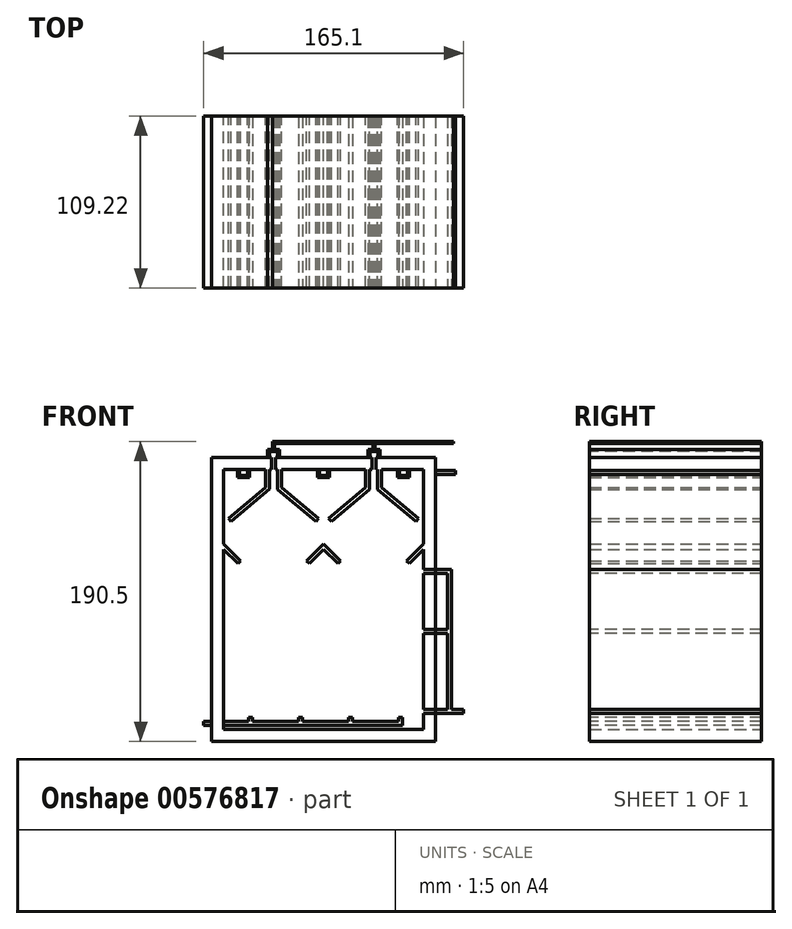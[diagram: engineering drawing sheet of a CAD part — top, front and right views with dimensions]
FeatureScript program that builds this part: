
annotation { "Feature Type Name" : "Feature", "Feature Type Description" : "" }
export const myFeature = defineFeature(function(context is Context, id is Id, definition is map)
    precondition{}
    {
        {
            var Q0;
            Q0=qCreatedBy(makeId("Front.planeOp"),FACE);
            var sketch = newSketch(context, id + "F0", { "sketchPlane" : qUnion([Q0])});
            skLineSegment(sketch, "E0", {"start": v(0, 0) * mm, "end": v(0, 165.1) * mm});
            skLineSegment(sketch, "E1", {"start": v(0, 165.1) * mm, "end": v(127, 165.1) * mm});
            skLineSegment(sketch, "E2", {"start": v(127, 165.1) * mm, "end": v(127, 0) * mm});
            skLineSegment(sketch, "E3", {"start": v(127, 0) * mm, "end": v(0, 0) * mm});
            skLineSegment(sketch, "E4.0", {"start": v(-7.62, -7.62) * mm, "end": v(-7.62, 172.72) * mm});
            skLineSegment(sketch, "E5.0", {"start": v(134.62, -7.62) * mm, "end": v(-7.62, -7.62) * mm});
            skLineSegment(sketch, "E6.0", {"start": v(134.62, 172.72) * mm, "end": v(134.62, -7.62) * mm});
            skLineSegment(sketch, "E7.0", {"start": v(-7.62, 172.72) * mm, "end": v(134.62, 172.72) * mm});
            skSolve(sketch);
        }
        {
            var Q0;
            Q0 = qSketchRegion(id + "F0", true);
            extrude(context, id + "F1", {"entities" : qUnion([Q0]), "depth" : 109.22 * mm, "offsetDistance" : 25.4 * mm});
        }
        {
            var Q0;
            Q0=qCreatedBy(makeId("Front.planeOp"),FACE);
            var sketch = newSketch(context, id + "F2", { "sketchPlane" : qUnion([Q0])});
            skLineSegment(sketch, "E8", {"start": v(0, 0) * mm, "end": v(0, 114.3) * mm, "construction": true});
            skLineSegment(sketch, "E9", {"start": v(34.14, 165.23) * mm, "end": v(34.14, 152.53) * mm});
            skLineSegment(sketch, "E10", {"start": v(34.14, 152.53) * mm, "end": v(58.5, 132.1) * mm});
            skLineSegment(sketch, "E11.0", {"start": v(29.06, 165.23) * mm, "end": v(29.06, 152.61) * mm});
            skLineSegment(sketch, "E12", {"start": v(29.06, 152.61) * mm, "end": v(4.61, 132.1) * mm});
            skLineSegment(sketch, "E13.MirrorCS", {"start": v(92.62, 152.45) * mm, "end": v(68.3, 132.04) * mm});
            skLineSegment(sketch, "E14.MirrorCS", {"start": v(92.62, 165.15) * mm, "end": v(92.62, 152.45) * mm});
            skLineSegment(sketch, "E15.MirrorCS", {"start": v(97.7, 165.14) * mm, "end": v(97.7, 152.44) * mm});
            skLineSegment(sketch, "E16.MirrorCS", {"start": v(97.7, 152.44) * mm, "end": v(122.02, 132.03) * mm});
            skLineSegment(sketch, "E17", {"start": v(0, 114.3) * mm, "end": v(8.98, 105.32) * mm});
            skLineSegment(sketch, "E18.MirrorCS", {"start": v(127, 114.3) * mm, "end": v(118.02, 105.32) * mm});
            skLineSegment(sketch, "E19", {"start": v(63.5, 114.3) * mm, "end": v(54.52, 105.32) * mm});
            skLineSegment(sketch, "E20", {"start": v(63.5, 114.3) * mm, "end": v(72.48, 105.32) * mm});
            skLineSegment(sketch, "E21", {"start": v(63.35, 165.19) * mm, "end": v(63.35, 0) * mm, "construction": true});
            skLineSegment(sketch, "E22.0", {"start": v(0, 117.9) * mm, "end": v(10.78, 107.12) * mm});
            skLineSegment(sketch, "E23.0", {"start": v(127, 117.9) * mm, "end": v(116.22, 107.12) * mm});
            skLineSegment(sketch, "E24.0", {"start": v(63.5, 117.9) * mm, "end": v(52.72, 107.12) * mm});
            skLineSegment(sketch, "E25.0", {"start": v(63.5, 117.9) * mm, "end": v(74.28, 107.12) * mm});
            skLineSegment(sketch, "E26", {"start": v(127, 114.3) * mm, "end": v(127, 121.24) * mm, "construction": true});
            skLineSegment(sketch, "E27", {"start": v(118.02, 105.32) * mm, "end": v(116.22, 107.12) * mm});
            skLineSegment(sketch, "E28", {"start": v(72.48, 105.32) * mm, "end": v(74.28, 107.12) * mm});
            skLineSegment(sketch, "E29", {"start": v(54.52, 105.32) * mm, "end": v(52.72, 107.12) * mm});
            skLineSegment(sketch, "E30", {"start": v(8.98, 105.32) * mm, "end": v(10.78, 107.12) * mm, "construction": true});
            skLineSegment(sketch, "E31.0", {"start": v(90.08, 153.63) * mm, "end": v(66.67, 133.98) * mm});
            skLineSegment(sketch, "E32", {"start": v(0, 165.27) * mm, "end": v(127, 165.1) * mm, "construction": true});
            skLineSegment(sketch, "E33", {"start": v(0, 0) * mm, "end": v(127, 0) * mm, "construction": true});
            skLineSegment(sketch, "E34", {"start": v(127, 165.1) * mm, "end": v(127, 0) * mm, "construction": true});
            skLineSegment(sketch, "E35.0", {"start": v(100.24, 153.62) * mm, "end": v(123.66, 133.98) * mm});
            skLineSegment(sketch, "E36.0", {"start": v(90.08, 165.22) * mm, "end": v(90.08, 153.63) * mm});
            skLineSegment(sketch, "E37.0", {"start": v(100.24, 165.24) * mm, "end": v(100.24, 153.62) * mm});
            skLineSegment(sketch, "E38", {"start": v(66.67, 133.98) * mm, "end": v(68.3, 132.04) * mm});
            skLineSegment(sketch, "E39", {"start": v(122.02, 132.03) * mm, "end": v(123.66, 133.98) * mm});
            skLineSegment(sketch, "E40.MirrorCS", {"start": v(36.6, 153.63) * mm, "end": v(60.02, 133.98) * mm});
            skLineSegment(sketch, "E41.MirrorCS", {"start": v(60.02, 133.98) * mm, "end": v(58.4, 132.04) * mm});
            skLineSegment(sketch, "E42.MirrorCS", {"start": v(36.6, 165.22) * mm, "end": v(36.6, 153.63) * mm});
            skLineSegment(sketch, "E43.MirrorCS", {"start": v(26.45, 165.24) * mm, "end": v(26.45, 153.62) * mm});
            skLineSegment(sketch, "E44.MirrorCS", {"start": v(26.45, 153.62) * mm, "end": v(3.04, 133.98) * mm});
            skLineSegment(sketch, "E45.MirrorCS", {"start": v(4.61, 132.1) * mm, "end": v(3.04, 133.98) * mm});
            skLineSegment(sketch, "E46", {"start": v(0, 165.27) * mm, "end": v(0, 0) * mm, "construction": true});
            skLineSegment(sketch, "E47", {"start": v(8.98, 105.32) * mm, "end": v(10.78, 107.12) * mm});
            skLineSegment(sketch, "E48", {"start": v(127, 114.3) * mm, "end": v(127, 117.9) * mm});
            skLineSegment(sketch, "E49", {"start": v(0, 114.3) * mm, "end": v(0, 117.9) * mm});
            skLineSegment(sketch, "E50", {"start": v(90.08, 165.22) * mm, "end": v(92.62, 165.15) * mm});
            skLineSegment(sketch, "E51", {"start": v(97.7, 165.14) * mm, "end": v(100.24, 165.24) * mm});
            skLineSegment(sketch, "E52", {"start": v(26.45, 165.24) * mm, "end": v(29.06, 165.23) * mm});
            skLineSegment(sketch, "E53", {"start": v(34.14, 165.23) * mm, "end": v(36.6, 165.22) * mm});
            skSolve(sketch);
        }
        {
            var Q0;
            Q0 = qSketchRegion(id + "F2", true);
            extrude(context, id + "F3", {"entities" : qUnion([Q0]), "operationType" : NewBodyOperationType.ADD, "depth" : 109.22 * mm, "offsetDistance" : 25.4 * mm});
        }
        {
            var Q0;
            Q0=qCreatedBy(makeId("Front.planeOp"),FACE);
            var sketch = newSketch(context, id + "F4", { "sketchPlane" : qUnion([Q0])});
            skLineSegment(sketch, "E54.0", {"start": v(36.6, 165.1) * mm, "end": v(90.08, 165.1) * mm, "construction": true});
            skLineSegment(sketch, "E55.2.0.0", {"start": v(161.14, 160.02) * mm, "end": v(161.14, 165.1) * mm});
            skLineSegment(sketch, "E55.2.0.1", {"start": v(164.95, 160.02) * mm, "end": v(168.76, 160.02) * mm});
            skLineSegment(sketch, "E55.2.0.2", {"start": v(164.95, 165.1) * mm, "end": v(164.95, 160.02) * mm, "construction": true});
            skLineSegment(sketch, "E55.2.0.3", {"start": v(168.76, 160.02) * mm, "end": v(168.76, 165.1) * mm});
            skLineSegment(sketch, "E55.2.0.4", {"start": v(164.95, 160.02) * mm, "end": v(161.14, 160.02) * mm});
            skLineSegment(sketch, "E56.1.0.0", {"start": v(16.36, 160.02) * mm, "end": v(16.36, 165.1) * mm});
            skLineSegment(sketch, "E56.1.0.1", {"start": v(12.55, 160.02) * mm, "end": v(16.36, 160.02) * mm});
            skLineSegment(sketch, "E56.1.0.2", {"start": v(8.74, 160.02) * mm, "end": v(8.74, 165.1) * mm});
            skLineSegment(sketch, "E56.1.0.3", {"start": v(12.55, 165.1) * mm, "end": v(12.55, 160.02) * mm, "construction": true});
            skLineSegment(sketch, "E56.1.0.4", {"start": v(12.55, 160.02) * mm, "end": v(8.74, 160.02) * mm});
            skLineSegment(sketch, "E57", {"start": v(8.74, 165.1) * mm, "end": v(10, 165.1) * mm});
            skLineSegment(sketch, "E58", {"start": v(10, 165.1) * mm, "end": v(10, 161.3) * mm});
            skLineSegment(sketch, "E59", {"start": v(10, 161.3) * mm, "end": v(15.09, 161.3) * mm});
            skLineSegment(sketch, "E60", {"start": v(15.09, 161.3) * mm, "end": v(15.09, 165.1) * mm});
            skLineSegment(sketch, "E61", {"start": v(15.09, 165.1) * mm, "end": v(16.36, 165.1) * mm});
            skLineSegment(sketch, "E62.1.0.0", {"start": v(67.16, 160.02) * mm, "end": v(67.16, 165.1) * mm});
            skLineSegment(sketch, "E62.1.0.1", {"start": v(63.35, 165.1) * mm, "end": v(63.35, 160.02) * mm, "construction": true});
            skLineSegment(sketch, "E62.1.0.2", {"start": v(59.54, 160.02) * mm, "end": v(59.54, 165.1) * mm});
            skLineSegment(sketch, "E62.1.0.3", {"start": v(65.89, 161.3) * mm, "end": v(65.89, 165.1) * mm});
            skLineSegment(sketch, "E62.1.0.4", {"start": v(63.35, 160.02) * mm, "end": v(67.16, 160.02) * mm});
            skLineSegment(sketch, "E62.1.0.5", {"start": v(63.35, 160.02) * mm, "end": v(59.54, 160.02) * mm});
            skLineSegment(sketch, "E62.1.0.6", {"start": v(60.8, 161.3) * mm, "end": v(65.89, 161.3) * mm});
            skLineSegment(sketch, "E62.1.0.7", {"start": v(60.8, 165.1) * mm, "end": v(60.8, 161.3) * mm});
            skLineSegment(sketch, "E62.1.0.8", {"start": v(65.89, 165.1) * mm, "end": v(67.16, 165.1) * mm});
            skLineSegment(sketch, "E62.1.0.9", {"start": v(59.54, 165.1) * mm, "end": v(60.8, 165.1) * mm});
            skLineSegment(sketch, "E62.1.0.10", {"start": v(59.54, 165.1) * mm, "end": v(60.8, 165.1) * mm});
            skLineSegment(sketch, "E62.2.0.0", {"start": v(117.96, 160.02) * mm, "end": v(117.96, 165.1) * mm});
            skLineSegment(sketch, "E62.2.0.1", {"start": v(114.15, 165.1) * mm, "end": v(114.15, 160.02) * mm, "construction": true});
            skLineSegment(sketch, "E62.2.0.2", {"start": v(110.34, 160.02) * mm, "end": v(110.34, 165.1) * mm});
            skLineSegment(sketch, "E62.2.0.3", {"start": v(116.69, 161.3) * mm, "end": v(116.69, 165.1) * mm});
            skLineSegment(sketch, "E62.2.0.4", {"start": v(114.15, 160.02) * mm, "end": v(117.96, 160.02) * mm});
            skLineSegment(sketch, "E62.2.0.5", {"start": v(114.15, 160.02) * mm, "end": v(110.34, 160.02) * mm});
            skLineSegment(sketch, "E62.2.0.6", {"start": v(111.6, 161.3) * mm, "end": v(116.69, 161.3) * mm});
            skLineSegment(sketch, "E62.2.0.7", {"start": v(111.6, 165.1) * mm, "end": v(111.6, 161.3) * mm});
            skLineSegment(sketch, "E62.2.0.8", {"start": v(116.69, 165.1) * mm, "end": v(117.96, 165.1) * mm});
            skLineSegment(sketch, "E62.2.0.9", {"start": v(110.34, 165.1) * mm, "end": v(111.6, 165.1) * mm});
            skLineSegment(sketch, "E62.2.0.10", {"start": v(110.34, 165.1) * mm, "end": v(111.6, 165.1) * mm});
            skLineSegment(sketch, "E62.direction1", {"start": v(8.74, 160.02) * mm, "end": v(59.54, 160.02) * mm, "construction": true});
            skSolve(sketch);
        }
        {
            var Q0;
            Q0 = qSketchRegion(id + "F4", true);
            extrude(context, id + "F5", {"entities" : qUnion([Q0]), "depth" : 109.22 * mm, "offsetDistance" : 25.4 * mm});
        }
        {
            var Q0;
            Q0=makeQuery(id+"F3.boolean.opBoolean","MERGE",FACE,{"derivedFrom":[makeQuery(id+"F1.opExtrude","CAP_FACE",FACE,{"disambiguationData":[OSD([sQuery(id+"F0.wireOp",EDGE,"E0"),sQuery(id+"F0.wireOp",EDGE,"E1"),sQuery(id+"F0.wireOp",EDGE,"E2"),sQuery(id+"F0.wireOp",EDGE,"E3"),sQuery(id+"F0.wireOp",EDGE,"E4.0"),sQuery(id+"F0.wireOp",EDGE,"E5.0"),sQuery(id+"F0.wireOp",EDGE,"E6.0"),sQuery(id+"F0.wireOp",EDGE,"E7.0")])],"isStart":false}),makeQuery(id+"F3.opExtrude","CAP_FACE",FACE,{"disambiguationData":[OSD([sQuery(id+"F2.wireOp",EDGE,"E9"),sQuery(id+"F2.wireOp",EDGE,"E10"),sQuery(id+"F2.wireOp",EDGE,"E40.MirrorCS"),sQuery(id+"F2.wireOp",EDGE,"E41.MirrorCS"),sQuery(id+"F2.wireOp",EDGE,"E42.MirrorCS"),sQuery(id+"F2.wireOp",EDGE,"E53")])],"isStart":false}),makeQuery(id+"F3.opExtrude","CAP_FACE",FACE,{"disambiguationData":[OSD([sQuery(id+"F2.wireOp",EDGE,"E11.0"),sQuery(id+"F2.wireOp",EDGE,"E12"),sQuery(id+"F2.wireOp",EDGE,"E43.MirrorCS"),sQuery(id+"F2.wireOp",EDGE,"E44.MirrorCS"),sQuery(id+"F2.wireOp",EDGE,"E45.MirrorCS"),sQuery(id+"F2.wireOp",EDGE,"E52")])],"isStart":false}),makeQuery(id+"F3.opExtrude","CAP_FACE",FACE,{"disambiguationData":[OSD([sQuery(id+"F2.wireOp",EDGE,"E13.MirrorCS"),sQuery(id+"F2.wireOp",EDGE,"E14.MirrorCS"),sQuery(id+"F2.wireOp",EDGE,"E31.0"),sQuery(id+"F2.wireOp",EDGE,"E36.0"),sQuery(id+"F2.wireOp",EDGE,"E38"),sQuery(id+"F2.wireOp",EDGE,"E50")])],"isStart":false}),makeQuery(id+"F3.opExtrude","CAP_FACE",FACE,{"disambiguationData":[OSD([sQuery(id+"F2.wireOp",EDGE,"E15.MirrorCS"),sQuery(id+"F2.wireOp",EDGE,"E16.MirrorCS"),sQuery(id+"F2.wireOp",EDGE,"E35.0"),sQuery(id+"F2.wireOp",EDGE,"E37.0"),sQuery(id+"F2.wireOp",EDGE,"E39"),sQuery(id+"F2.wireOp",EDGE,"E51")])],"isStart":false}),makeQuery(id+"F3.opExtrude","CAP_FACE",FACE,{"disambiguationData":[OSD([sQuery(id+"F2.wireOp",EDGE,"E17"),sQuery(id+"F2.wireOp",EDGE,"E22.0"),sQuery(id+"F2.wireOp",EDGE,"E47"),sQuery(id+"F2.wireOp",EDGE,"E49")])],"isStart":false}),makeQuery(id+"F3.opExtrude","CAP_FACE",FACE,{"disambiguationData":[OSD([sQuery(id+"F2.wireOp",EDGE,"E18.MirrorCS"),sQuery(id+"F2.wireOp",EDGE,"E23.0"),sQuery(id+"F2.wireOp",EDGE,"E27"),sQuery(id+"F2.wireOp",EDGE,"E48")])],"isStart":false})]});
            var sketch = newSketch(context, id + "F6", { "sketchPlane" : qUnion([Q0])});
            skLineSegment(sketch, "E63", {"start": v(63.5, 172.72) * mm, "end": v(31.6, 172.72) * mm, "construction": true});
            skPoint(sketch, "E63.endSnap0", {"position": v(31.6, 165.1) * mm});
            skLineSegment(sketch, "E64", {"start": v(31.6, 172.72) * mm, "end": v(31.6, 165.1) * mm, "construction": true});
            skLineSegment(sketch, "E65.0", {"start": v(32.87, 172.72) * mm, "end": v(32.87, 165.1) * mm});
            skLineSegment(sketch, "E66.MirrorCS", {"start": v(30.33, 172.72) * mm, "end": v(30.33, 165.1) * mm});
            skLineSegment(sketch, "E67", {"start": v(30.33, 172.72) * mm, "end": v(32.87, 172.72) * mm});
            skLineSegment(sketch, "E68", {"start": v(30.33, 165.1) * mm, "end": v(32.87, 165.1) * mm});
            skLineSegment(sketch, "E69", {"start": v(63.5, 172.72) * mm, "end": v(63.5, 165.1) * mm, "construction": true});
            skLineSegment(sketch, "E70.MirrorCS", {"start": v(96.67, 165.1) * mm, "end": v(94.13, 165.1) * mm});
            skLineSegment(sketch, "E71.MirrorCS", {"start": v(96.67, 172.72) * mm, "end": v(94.13, 172.72) * mm});
            skLineSegment(sketch, "E72.MirrorCS", {"start": v(96.67, 172.72) * mm, "end": v(96.67, 165.1) * mm});
            skLineSegment(sketch, "E73.MirrorCS", {"start": v(94.13, 172.72) * mm, "end": v(94.13, 165.1) * mm});
            skLineSegment(sketch, "E74.MirrorCS", {"start": v(95.4, 172.72) * mm, "end": v(95.4, 165.1) * mm, "construction": true});
            skPoint(sketch, "E75.MirrorP", {"position": v(95.4, 165.1) * mm});
            skSolve(sketch);
        }
        {
            var Q0;
            Q0 = qSketchRegion(id + "F6", true);
            extrude(context, id + "F7", {"entities" : qUnion([Q0]), "operationType" : NewBodyOperationType.REMOVE, "endBound" : BoundingType.THROUGH_ALL, "oppositeDirection" : true, "depth" : 25.4 * mm, "offsetDistance" : 25.4 * mm});
        }
        {
            var Q0;
            {var subQ0=sQuery(id+"F2.wireOp",EDGE,"E40.MirrorCS");var subQ1=sQuery(id+"F2.wireOp",EDGE,"E36.0");var subQ2=sQuery(id+"F2.wireOp",EDGE,"E13.MirrorCS");var subQ3=sQuery(id+"F0.wireOp",EDGE,"E1");var subQ4=sQuery(id+"F2.wireOp",EDGE,"E38");var subQ5=sQuery(id+"F0.wireOp",EDGE,"E7.0");var subQ6=sQuery(id+"F2.wireOp",EDGE,"E31.0");var subQ7=sQuery(id+"F2.wireOp",EDGE,"E14.MirrorCS");var subQ8=sQuery(id+"F2.wireOp",EDGE,"E9");var subQ9=sQuery(id+"F2.wireOp",EDGE,"E10");var subQ10=sQuery(id+"F2.wireOp",EDGE,"E41.MirrorCS");var subQ11=sQuery(id+"F2.wireOp",EDGE,"E42.MirrorCS");Q0=makeQuery(id+"F7.boolean.opBoolean","SPLIT",FACE,{"disambiguationData":[TD([makeQuery(id+"F3.opExtrude","SWEPT_FACE",FACE,{"disambiguationData":[OSD([subQ8])]})])],"derivedFrom":makeQuery(id+"F3.boolean.opBoolean","MERGE",FACE,{"derivedFrom":[makeQuery(id+"F1.opExtrude","CAP_FACE",FACE,{"disambiguationData":[OSD([sQuery(id+"F0.wireOp",EDGE,"E0"),subQ3,sQuery(id+"F0.wireOp",EDGE,"E2"),sQuery(id+"F0.wireOp",EDGE,"E3"),sQuery(id+"F0.wireOp",EDGE,"E4.0"),sQuery(id+"F0.wireOp",EDGE,"E5.0"),sQuery(id+"F0.wireOp",EDGE,"E6.0"),subQ5])],"isStart":false}),makeQuery(id+"F3.opExtrude","CAP_FACE",FACE,{"disambiguationData":[OSD([subQ8,subQ9,subQ0,subQ10,subQ11,sQuery(id+"F2.wireOp",EDGE,"E53")])],"isStart":false}),makeQuery(id+"F3.opExtrude","CAP_FACE",FACE,{"disambiguationData":[OSD([sQuery(id+"F2.wireOp",EDGE,"E11.0"),sQuery(id+"F2.wireOp",EDGE,"E12"),sQuery(id+"F2.wireOp",EDGE,"E43.MirrorCS"),sQuery(id+"F2.wireOp",EDGE,"E44.MirrorCS"),sQuery(id+"F2.wireOp",EDGE,"E45.MirrorCS"),sQuery(id+"F2.wireOp",EDGE,"E52")])],"isStart":false}),makeQuery(id+"F3.opExtrude","CAP_FACE",FACE,{"disambiguationData":[OSD([subQ2,subQ7,subQ6,subQ1,subQ4,sQuery(id+"F2.wireOp",EDGE,"E50")])],"isStart":false}),makeQuery(id+"F3.opExtrude","CAP_FACE",FACE,{"disambiguationData":[OSD([sQuery(id+"F2.wireOp",EDGE,"E15.MirrorCS"),sQuery(id+"F2.wireOp",EDGE,"E16.MirrorCS"),sQuery(id+"F2.wireOp",EDGE,"E35.0"),sQuery(id+"F2.wireOp",EDGE,"E37.0"),sQuery(id+"F2.wireOp",EDGE,"E39"),sQuery(id+"F2.wireOp",EDGE,"E51")])],"isStart":false}),makeQuery(id+"F3.opExtrude","CAP_FACE",FACE,{"disambiguationData":[OSD([sQuery(id+"F2.wireOp",EDGE,"E17"),sQuery(id+"F2.wireOp",EDGE,"E22.0"),sQuery(id+"F2.wireOp",EDGE,"E47"),sQuery(id+"F2.wireOp",EDGE,"E49")])],"isStart":false}),makeQuery(id+"F3.opExtrude","CAP_FACE",FACE,{"disambiguationData":[OSD([sQuery(id+"F2.wireOp",EDGE,"E18.MirrorCS"),sQuery(id+"F2.wireOp",EDGE,"E23.0"),sQuery(id+"F2.wireOp",EDGE,"E27"),sQuery(id+"F2.wireOp",EDGE,"E48")])],"isStart":false})]})});}
            var sketch = newSketch(context, id + "F8", { "sketchPlane" : qUnion([Q0])});
            skLineSegment(sketch, "E76", {"start": v(32.87, 172.72) * mm, "end": v(35.4, 172.72) * mm});
            skLineSegment(sketch, "E77", {"start": v(35.4, 172.72) * mm, "end": v(35.4, 177.8) * mm});
            skLineSegment(sketch, "E78", {"start": v(35.4, 177.8) * mm, "end": v(34.14, 177.8) * mm});
            skLineSegment(sketch, "E79", {"start": v(34.14, 177.8) * mm, "end": v(29.06, 177.8) * mm});
            skLineSegment(sketch, "E80", {"start": v(29.06, 177.8) * mm, "end": v(27.79, 177.8) * mm});
            skLineSegment(sketch, "E81", {"start": v(27.79, 177.8) * mm, "end": v(27.79, 172.72) * mm});
            skLineSegment(sketch, "E82", {"start": v(27.79, 172.72) * mm, "end": v(29.06, 172.72) * mm});
            skLineSegment(sketch, "E83", {"start": v(29.06, 172.72) * mm, "end": v(29.06, 176.53) * mm});
            skLineSegment(sketch, "E84", {"start": v(29.06, 176.53) * mm, "end": v(34.14, 176.53) * mm});
            skLineSegment(sketch, "E85", {"start": v(34.14, 176.53) * mm, "end": v(34.14, 172.72) * mm});
            skLineSegment(sketch, "E86", {"start": v(63.5, 172.72) * mm, "end": v(63.5, 177.8) * mm, "construction": true});
            skLineSegment(sketch, "E87.MirrorCS", {"start": v(91.6, 177.8) * mm, "end": v(92.86, 177.8) * mm});
            skLineSegment(sketch, "E88.MirrorCS", {"start": v(97.94, 177.8) * mm, "end": v(99.21, 177.8) * mm});
            skLineSegment(sketch, "E89.MirrorCS", {"start": v(99.21, 172.72) * mm, "end": v(97.94, 172.72) * mm});
            skLineSegment(sketch, "E90.MirrorCS", {"start": v(94.13, 172.72) * mm, "end": v(91.6, 172.72) * mm});
            skLineSegment(sketch, "E91.MirrorCS", {"start": v(91.6, 172.72) * mm, "end": v(91.6, 177.8) * mm});
            skLineSegment(sketch, "E92.MirrorCS", {"start": v(92.86, 176.53) * mm, "end": v(92.86, 172.72) * mm});
            skLineSegment(sketch, "E93.MirrorCS", {"start": v(97.94, 176.53) * mm, "end": v(92.86, 176.53) * mm});
            skLineSegment(sketch, "E94.MirrorCS", {"start": v(99.21, 177.8) * mm, "end": v(99.21, 172.72) * mm});
            skLineSegment(sketch, "E95.MirrorCS", {"start": v(97.94, 172.72) * mm, "end": v(97.94, 176.53) * mm});
            skLineSegment(sketch, "E96.MirrorCS", {"start": v(92.86, 177.8) * mm, "end": v(97.94, 177.8) * mm});
            skSolve(sketch);
        }
        {
            var Q0;
            Q0 = qSketchRegion(id + "F8", true);
            extrude(context, id + "F9", {"entities" : qUnion([Q0]), "oppositeDirection" : true, "depth" : 109.22 * mm, "offsetDistance" : 25.4 * mm});
        }
        {
            var Q0;
            {var subQ0=sQuery(id+"F2.wireOp",EDGE,"E44.MirrorCS");var subQ1=sQuery(id+"F2.wireOp",EDGE,"E35.0");var subQ2=sQuery(id+"F2.wireOp",EDGE,"E22.0");var subQ3=sQuery(id+"F2.wireOp",EDGE,"E15.MirrorCS");var subQ4=sQuery(id+"F0.wireOp",EDGE,"E2");var subQ5=sQuery(id+"F2.wireOp",EDGE,"E47");var subQ6=sQuery(id+"F2.wireOp",EDGE,"E37.0");var subQ7=sQuery(id+"F0.wireOp",EDGE,"E1");var subQ8=sQuery(id+"F2.wireOp",EDGE,"E45.MirrorCS");var subQ9=sQuery(id+"F2.wireOp",EDGE,"E39");var subQ10=sQuery(id+"F2.wireOp",EDGE,"E16.MirrorCS");var subQ11=sQuery(id+"F0.wireOp",EDGE,"E3");var subQ12=sQuery(id+"F0.wireOp",EDGE,"E0");var subQ13=sQuery(id+"F2.wireOp",EDGE,"E17");var subQ14=sQuery(id+"F0.wireOp",EDGE,"E4.0");var subQ15=sQuery(id+"F0.wireOp",EDGE,"E5.0");var subQ16=sQuery(id+"F0.wireOp",EDGE,"E6.0");var subQ17=sQuery(id+"F2.wireOp",EDGE,"E43.MirrorCS");var subQ18=sQuery(id+"F2.wireOp",EDGE,"E18.MirrorCS");var subQ19=sQuery(id+"F0.wireOp",EDGE,"E7.0");var subQ20=sQuery(id+"F2.wireOp",EDGE,"E23.0");var subQ21=sQuery(id+"F2.wireOp",EDGE,"E11.0");var subQ22=sQuery(id+"F2.wireOp",EDGE,"E27");var subQ23=sQuery(id+"F2.wireOp",EDGE,"E12");Q0=makeQuery(id+"F7.boolean.opBoolean","SPLIT",FACE,{"disambiguationData":[TD([makeQuery(id+"F1.opExtrude","SWEPT_FACE",FACE,{"disambiguationData":[OSD([subQ12])]})])],"derivedFrom":makeQuery(id+"F3.boolean.opBoolean","MERGE",FACE,{"derivedFrom":[makeQuery(id+"F1.opExtrude","CAP_FACE",FACE,{"disambiguationData":[OSD([subQ12,subQ7,subQ4,subQ11,subQ14,subQ15,subQ16,subQ19])],"isStart":false}),makeQuery(id+"F3.opExtrude","CAP_FACE",FACE,{"disambiguationData":[OSD([sQuery(id+"F2.wireOp",EDGE,"E9"),sQuery(id+"F2.wireOp",EDGE,"E10"),sQuery(id+"F2.wireOp",EDGE,"E40.MirrorCS"),sQuery(id+"F2.wireOp",EDGE,"E41.MirrorCS"),sQuery(id+"F2.wireOp",EDGE,"E42.MirrorCS"),sQuery(id+"F2.wireOp",EDGE,"E53")])],"isStart":false}),makeQuery(id+"F3.opExtrude","CAP_FACE",FACE,{"disambiguationData":[OSD([subQ21,subQ23,subQ17,subQ0,subQ8,sQuery(id+"F2.wireOp",EDGE,"E52")])],"isStart":false}),makeQuery(id+"F3.opExtrude","CAP_FACE",FACE,{"disambiguationData":[OSD([sQuery(id+"F2.wireOp",EDGE,"E13.MirrorCS"),sQuery(id+"F2.wireOp",EDGE,"E14.MirrorCS"),sQuery(id+"F2.wireOp",EDGE,"E31.0"),sQuery(id+"F2.wireOp",EDGE,"E36.0"),sQuery(id+"F2.wireOp",EDGE,"E38"),sQuery(id+"F2.wireOp",EDGE,"E50")])],"isStart":false}),makeQuery(id+"F3.opExtrude","CAP_FACE",FACE,{"disambiguationData":[OSD([subQ3,subQ10,subQ1,subQ6,subQ9,sQuery(id+"F2.wireOp",EDGE,"E51")])],"isStart":false}),makeQuery(id+"F3.opExtrude","CAP_FACE",FACE,{"disambiguationData":[OSD([subQ13,subQ2,subQ5,sQuery(id+"F2.wireOp",EDGE,"E49")])],"isStart":false}),makeQuery(id+"F3.opExtrude","CAP_FACE",FACE,{"disambiguationData":[OSD([subQ18,subQ20,subQ22,sQuery(id+"F2.wireOp",EDGE,"E48")])],"isStart":false})]})});}
            var sketch = newSketch(context, id + "F10", { "sketchPlane" : qUnion([Q0])});
            skLineSegment(sketch, "E97.top", {"start": v(1.16, 2.54) * mm, "end": v(113.56, 2.54) * mm});
            skLineSegment(sketch, "E98.top", {"start": v(1.16, 5.08) * mm, "end": v(113.56, 5.08) * mm});
            skLineSegment(sketch, "E99", {"start": v(1.16, 5.08) * mm, "end": v(17.04, 5.08) * mm});
            skLineSegment(sketch, "E100", {"start": v(17.04, 5.08) * mm, "end": v(48.79, 5.08) * mm});
            skLineSegment(sketch, "E101", {"start": v(48.79, 5.08) * mm, "end": v(80.54, 5.08) * mm});
            skLineSegment(sketch, "E102", {"start": v(80.54, 5.08) * mm, "end": v(112.29, 5.08) * mm});
            skLineSegment(sketch, "E103", {"start": v(17.04, 5.08) * mm, "end": v(15.77, 5.08) * mm});
            skLineSegment(sketch, "E104", {"start": v(15.77, 5.08) * mm, "end": v(15.77, 7.62) * mm});
            skLineSegment(sketch, "E105", {"start": v(15.77, 7.62) * mm, "end": v(18.3, 7.62) * mm});
            skLineSegment(sketch, "E106", {"start": v(18.3, 7.62) * mm, "end": v(18.3, 5.08) * mm});
            skLineSegment(sketch, "E107.1.0.0", {"start": v(47.52, 7.62) * mm, "end": v(50.06, 7.62) * mm});
            skLineSegment(sketch, "E107.1.0.1", {"start": v(47.52, 5.08) * mm, "end": v(47.52, 7.62) * mm});
            skLineSegment(sketch, "E107.1.0.2", {"start": v(50.06, 7.62) * mm, "end": v(50.06, 5.08) * mm});
            skLineSegment(sketch, "E107.2.0.0", {"start": v(79.27, 7.62) * mm, "end": v(81.8, 7.62) * mm});
            skLineSegment(sketch, "E107.2.0.1", {"start": v(79.27, 5.08) * mm, "end": v(79.27, 7.62) * mm});
            skLineSegment(sketch, "E107.2.0.2", {"start": v(81.8, 7.62) * mm, "end": v(81.8, 5.08) * mm});
            skLineSegment(sketch, "E107.3.0.0", {"start": v(111.02, 7.62) * mm, "end": v(113.56, 7.62) * mm});
            skLineSegment(sketch, "E107.3.0.1", {"start": v(111.02, 5.08) * mm, "end": v(111.02, 7.62) * mm});
            skLineSegment(sketch, "E107.3.0.2", {"start": v(113.56, 7.62) * mm, "end": v(113.56, 5.08) * mm});
            skLineSegment(sketch, "E107.direction1", {"start": v(15.77, 7.62) * mm, "end": v(47.52, 7.62) * mm, "construction": true});
            skLineSegment(sketch, "E108", {"start": v(1.16, 2.54) * mm, "end": v(0, 2.54) * mm});
            skLineSegment(sketch, "E109", {"start": v(0, 2.54) * mm, "end": v(0, 5.08) * mm});
            skLineSegment(sketch, "E110", {"start": v(0, 5.08) * mm, "end": v(1.16, 5.08) * mm});
            skLineSegment(sketch, "E111", {"start": v(113.56, 5.08) * mm, "end": v(113.56, 2.54) * mm});
            skLineSegment(sketch, "E112", {"start": v(-7.62, 5.08) * mm, "end": v(-12.7, 5.08) * mm});
            skLineSegment(sketch, "E113", {"start": v(-12.7, 5.08) * mm, "end": v(-12.7, 2.54) * mm});
            skLineSegment(sketch, "E114", {"start": v(-12.7, 2.54) * mm, "end": v(-7.62, 2.54) * mm});
            skLineSegment(sketch, "E115", {"start": v(-7.62, 2.54) * mm, "end": v(-7.62, 5.08) * mm});
            skSolve(sketch);
        }
        {
            var Q0;
            Q0 = qSketchRegion(id + "F10", true);
            extrude(context, id + "F11", {"entities" : qUnion([Q0]), "oppositeDirection" : true, "depth" : 109.22 * mm, "offsetDistance" : 25.4 * mm});
        }
        {
            var Q0;
            {var subQ0=sQuery(id+"F2.wireOp",EDGE,"E44.MirrorCS");var subQ1=sQuery(id+"F2.wireOp",EDGE,"E35.0");var subQ2=sQuery(id+"F2.wireOp",EDGE,"E22.0");var subQ3=sQuery(id+"F2.wireOp",EDGE,"E15.MirrorCS");var subQ4=sQuery(id+"F0.wireOp",EDGE,"E2");var subQ5=sQuery(id+"F2.wireOp",EDGE,"E47");var subQ6=sQuery(id+"F2.wireOp",EDGE,"E37.0");var subQ7=sQuery(id+"F0.wireOp",EDGE,"E1");var subQ8=sQuery(id+"F2.wireOp",EDGE,"E45.MirrorCS");var subQ9=sQuery(id+"F2.wireOp",EDGE,"E39");var subQ10=sQuery(id+"F2.wireOp",EDGE,"E16.MirrorCS");var subQ11=sQuery(id+"F0.wireOp",EDGE,"E3");var subQ12=sQuery(id+"F0.wireOp",EDGE,"E0");var subQ13=sQuery(id+"F2.wireOp",EDGE,"E17");var subQ14=sQuery(id+"F0.wireOp",EDGE,"E4.0");var subQ15=sQuery(id+"F0.wireOp",EDGE,"E5.0");var subQ16=sQuery(id+"F0.wireOp",EDGE,"E6.0");var subQ17=sQuery(id+"F2.wireOp",EDGE,"E43.MirrorCS");var subQ18=sQuery(id+"F2.wireOp",EDGE,"E18.MirrorCS");var subQ19=sQuery(id+"F0.wireOp",EDGE,"E7.0");var subQ20=sQuery(id+"F2.wireOp",EDGE,"E23.0");var subQ21=sQuery(id+"F2.wireOp",EDGE,"E11.0");var subQ22=sQuery(id+"F2.wireOp",EDGE,"E27");var subQ23=sQuery(id+"F2.wireOp",EDGE,"E12");Q0=makeQuery(id+"F11.boolean.opBoolean","MERGE",FACE,{"derivedFrom":[makeQuery(id+"F7.boolean.opBoolean","SPLIT",FACE,{"disambiguationData":[TD([makeQuery(id+"F1.opExtrude","SWEPT_FACE",FACE,{"disambiguationData":[OSD([subQ12])]})])],"derivedFrom":makeQuery(id+"F3.boolean.opBoolean","MERGE",FACE,{"derivedFrom":[makeQuery(id+"F1.opExtrude","CAP_FACE",FACE,{"disambiguationData":[OSD([subQ12,subQ7,subQ4,subQ11,subQ14,subQ15,subQ16,subQ19])],"isStart":false}),makeQuery(id+"F3.opExtrude","CAP_FACE",FACE,{"disambiguationData":[OSD([sQuery(id+"F2.wireOp",EDGE,"E9"),sQuery(id+"F2.wireOp",EDGE,"E10"),sQuery(id+"F2.wireOp",EDGE,"E40.MirrorCS"),sQuery(id+"F2.wireOp",EDGE,"E41.MirrorCS"),sQuery(id+"F2.wireOp",EDGE,"E42.MirrorCS"),sQuery(id+"F2.wireOp",EDGE,"E53")])],"isStart":false}),makeQuery(id+"F3.opExtrude","CAP_FACE",FACE,{"disambiguationData":[OSD([subQ21,subQ23,subQ17,subQ0,subQ8,sQuery(id+"F2.wireOp",EDGE,"E52")])],"isStart":false}),makeQuery(id+"F3.opExtrude","CAP_FACE",FACE,{"disambiguationData":[OSD([sQuery(id+"F2.wireOp",EDGE,"E13.MirrorCS"),sQuery(id+"F2.wireOp",EDGE,"E14.MirrorCS"),sQuery(id+"F2.wireOp",EDGE,"E31.0"),sQuery(id+"F2.wireOp",EDGE,"E36.0"),sQuery(id+"F2.wireOp",EDGE,"E38"),sQuery(id+"F2.wireOp",EDGE,"E50")])],"isStart":false}),makeQuery(id+"F3.opExtrude","CAP_FACE",FACE,{"disambiguationData":[OSD([subQ3,subQ10,subQ1,subQ6,subQ9,sQuery(id+"F2.wireOp",EDGE,"E51")])],"isStart":false}),makeQuery(id+"F3.opExtrude","CAP_FACE",FACE,{"disambiguationData":[OSD([subQ13,subQ2,subQ5,sQuery(id+"F2.wireOp",EDGE,"E49")])],"isStart":false}),makeQuery(id+"F3.opExtrude","CAP_FACE",FACE,{"disambiguationData":[OSD([subQ18,subQ20,subQ22,sQuery(id+"F2.wireOp",EDGE,"E48")])],"isStart":false})]})}),makeQuery(id+"F11.opExtrude","CAP_FACE",FACE,{"disambiguationData":[OSD([sQuery(id+"F10.wireOp",EDGE,"E97.top"),sQuery(id+"F10.wireOp",EDGE,"E98.top"),sQuery(id+"F10.wireOp",EDGE,"E98.left"),sQuery(id+"F10.wireOp",EDGE,"E98.right"),sQuery(id+"F10.wireOp",EDGE,"E99"),sQuery(id+"F10.wireOp",EDGE,"E100"),sQuery(id+"F10.wireOp",EDGE,"E101"),sQuery(id+"F10.wireOp",EDGE,"E102"),sQuery(id+"F10.wireOp",EDGE,"E104"),sQuery(id+"F10.wireOp",EDGE,"E105"),sQuery(id+"F10.wireOp",EDGE,"E106"),sQuery(id+"F10.wireOp",EDGE,"E107.1.0.0"),sQuery(id+"F10.wireOp",EDGE,"E107.1.0.1"),sQuery(id+"F10.wireOp",EDGE,"E107.1.0.2"),sQuery(id+"F10.wireOp",EDGE,"E107.2.0.0"),sQuery(id+"F10.wireOp",EDGE,"E107.2.0.1"),sQuery(id+"F10.wireOp",EDGE,"E107.2.0.2"),sQuery(id+"F10.wireOp",EDGE,"E107.3.0.0"),sQuery(id+"F10.wireOp",EDGE,"E107.3.0.1"),sQuery(id+"F10.wireOp",EDGE,"E107.3.0.2")])],"isStart":true})]});}
            var sketch = newSketch(context, id + "F12", { "sketchPlane" : qUnion([Q0])});
            skLineSegment(sketch, "E116", {"start": v(127, 5.08) * mm, "end": v(127, 10.16) * mm});
            skLineSegment(sketch, "E117", {"start": v(127, 10.16) * mm, "end": v(134.62, 10.16) * mm});
            skLineSegment(sketch, "E118", {"start": v(134.62, 10.16) * mm, "end": v(134.62, 12.7) * mm});
            skLineSegment(sketch, "E119", {"start": v(134.62, 12.7) * mm, "end": v(127, 12.7) * mm});
            skLineSegment(sketch, "E120", {"start": v(127, 12.7) * mm, "end": v(127, 10.16) * mm});
            skLineSegment(sketch, "E121.direction1", {"start": v(127, 10.16) * mm, "end": v(127, 10.16) * mm});
            skLineSegment(sketch, "E121.direction2", {"start": v(127, 10.16) * mm, "end": v(127, 60.96) * mm, "construction": true});
            skLineSegment(sketch, "E122.0.0.1", {"start": v(127, 60.96) * mm, "end": v(134.62, 60.96) * mm});
            skLineSegment(sketch, "E122.3.0.1", {"start": v(134.62, 60.96) * mm, "end": v(134.62, 63.5) * mm});
            skLineSegment(sketch, "E122.6.0.1", {"start": v(134.62, 63.5) * mm, "end": v(127, 63.5) * mm});
            skLineSegment(sketch, "E122.9.0.1", {"start": v(127, 63.5) * mm, "end": v(127, 60.96) * mm});
            skLineSegment(sketch, "E122.0.1.1", {"start": v(127, 60.96) * mm, "end": v(134.62, 60.96) * mm});
            skLineSegment(sketch, "E122.3.1.1", {"start": v(134.62, 60.96) * mm, "end": v(134.62, 63.5) * mm});
            skLineSegment(sketch, "E122.6.1.1", {"start": v(134.62, 63.5) * mm, "end": v(127, 63.5) * mm});
            skLineSegment(sketch, "E122.9.1.1", {"start": v(127, 63.5) * mm, "end": v(127, 60.96) * mm});
            skLineSegment(sketch, "E122.0.2.1", {"start": v(127, 60.96) * mm, "end": v(134.62, 60.96) * mm});
            skLineSegment(sketch, "E122.3.2.1", {"start": v(134.62, 60.96) * mm, "end": v(134.62, 63.5) * mm});
            skLineSegment(sketch, "E122.6.2.1", {"start": v(134.62, 63.5) * mm, "end": v(127, 63.5) * mm});
            skLineSegment(sketch, "E122.9.2.1", {"start": v(127, 63.5) * mm, "end": v(127, 60.96) * mm});
            skLineSegment(sketch, "E123.0.1.0", {"start": v(127, 99.06) * mm, "end": v(134.62, 99.06) * mm});
            skLineSegment(sketch, "E123.0.1.1", {"start": v(134.62, 101.6) * mm, "end": v(127, 101.6) * mm});
            skLineSegment(sketch, "E123.0.1.2", {"start": v(134.62, 101.6) * mm, "end": v(127, 101.6) * mm});
            skLineSegment(sketch, "E123.0.1.3", {"start": v(127, 99.06) * mm, "end": v(134.62, 99.06) * mm});
            skLineSegment(sketch, "E123.0.1.4", {"start": v(134.62, 101.6) * mm, "end": v(127, 101.6) * mm});
            skLineSegment(sketch, "E123.0.1.5", {"start": v(127, 99.06) * mm, "end": v(134.62, 99.06) * mm});
            skLineSegment(sketch, "E123.0.1.6", {"start": v(134.62, 99.06) * mm, "end": v(134.62, 101.6) * mm});
            skLineSegment(sketch, "E123.0.1.7", {"start": v(127, 101.6) * mm, "end": v(127, 99.06) * mm});
            skLineSegment(sketch, "E123.0.1.8", {"start": v(127, 101.6) * mm, "end": v(127, 99.06) * mm});
            skLineSegment(sketch, "E123.0.1.9", {"start": v(134.62, 99.06) * mm, "end": v(134.62, 101.6) * mm});
            skLineSegment(sketch, "E123.0.1.10", {"start": v(134.62, 99.06) * mm, "end": v(134.62, 101.6) * mm});
            skLineSegment(sketch, "E123.0.1.11", {"start": v(127, 101.6) * mm, "end": v(127, 99.06) * mm});
            skLineSegment(sketch, "E123.1.1.0", {"start": v(127, 99.06) * mm, "end": v(134.62, 99.06) * mm});
            skLineSegment(sketch, "E123.1.1.1", {"start": v(134.62, 101.6) * mm, "end": v(127, 101.6) * mm});
            skLineSegment(sketch, "E123.1.1.2", {"start": v(134.62, 101.6) * mm, "end": v(127, 101.6) * mm});
            skLineSegment(sketch, "E123.1.1.3", {"start": v(127, 99.06) * mm, "end": v(134.62, 99.06) * mm});
            skLineSegment(sketch, "E123.1.1.4", {"start": v(134.62, 101.6) * mm, "end": v(127, 101.6) * mm});
            skLineSegment(sketch, "E123.1.1.5", {"start": v(127, 99.06) * mm, "end": v(134.62, 99.06) * mm});
            skLineSegment(sketch, "E123.1.1.6", {"start": v(134.62, 99.06) * mm, "end": v(134.62, 101.6) * mm});
            skLineSegment(sketch, "E123.1.1.7", {"start": v(127, 101.6) * mm, "end": v(127, 99.06) * mm});
            skLineSegment(sketch, "E123.1.1.8", {"start": v(127, 101.6) * mm, "end": v(127, 99.06) * mm});
            skLineSegment(sketch, "E123.1.1.9", {"start": v(134.62, 99.06) * mm, "end": v(134.62, 101.6) * mm});
            skLineSegment(sketch, "E123.1.1.10", {"start": v(134.62, 99.06) * mm, "end": v(134.62, 101.6) * mm});
            skLineSegment(sketch, "E123.1.1.11", {"start": v(127, 101.6) * mm, "end": v(127, 99.06) * mm});
            skLineSegment(sketch, "E123.2.1.0", {"start": v(127, 99.06) * mm, "end": v(134.62, 99.06) * mm});
            skLineSegment(sketch, "E123.2.1.1", {"start": v(134.62, 101.6) * mm, "end": v(127, 101.6) * mm});
            skLineSegment(sketch, "E123.2.1.2", {"start": v(134.62, 101.6) * mm, "end": v(127, 101.6) * mm});
            skLineSegment(sketch, "E123.2.1.3", {"start": v(127, 99.06) * mm, "end": v(134.62, 99.06) * mm});
            skLineSegment(sketch, "E123.2.1.4", {"start": v(134.62, 101.6) * mm, "end": v(127, 101.6) * mm});
            skLineSegment(sketch, "E123.2.1.5", {"start": v(127, 99.06) * mm, "end": v(134.62, 99.06) * mm});
            skLineSegment(sketch, "E123.2.1.6", {"start": v(134.62, 99.06) * mm, "end": v(134.62, 101.6) * mm});
            skLineSegment(sketch, "E123.2.1.7", {"start": v(127, 101.6) * mm, "end": v(127, 99.06) * mm});
            skLineSegment(sketch, "E123.2.1.8", {"start": v(127, 101.6) * mm, "end": v(127, 99.06) * mm});
            skLineSegment(sketch, "E123.2.1.9", {"start": v(134.62, 99.06) * mm, "end": v(134.62, 101.6) * mm});
            skLineSegment(sketch, "E123.2.1.10", {"start": v(134.62, 99.06) * mm, "end": v(134.62, 101.6) * mm});
            skLineSegment(sketch, "E123.2.1.11", {"start": v(127, 101.6) * mm, "end": v(127, 99.06) * mm});
            skLineSegment(sketch, "E123.direction1", {"start": v(127, 60.96) * mm, "end": v(127, 60.96) * mm});
            skLineSegment(sketch, "E123.direction2", {"start": v(127, 60.96) * mm, "end": v(127, 99.06) * mm, "construction": true});
            skSolve(sketch);
        }
        {
            var Q0;
            Q0 = qSketchRegion(id + "F12", true);
            extrude(context, id + "F13", {"entities" : qUnion([Q0]), "operationType" : NewBodyOperationType.REMOVE, "endBound" : BoundingType.THROUGH_ALL, "oppositeDirection" : true, "depth" : 25.4 * mm, "offsetDistance" : 25.4 * mm});
        }
        {
            var Q0;
            Q0=makeQuery(id+"F9.opExtrude","CAP_FACE",FACE,{"disambiguationData":[OSD([sQuery(id+"F8.wireOp",EDGE,"E76"),sQuery(id+"F8.wireOp",EDGE,"E77"),sQuery(id+"F8.wireOp",EDGE,"E78"),sQuery(id+"F8.wireOp",EDGE,"E79"),sQuery(id+"F8.wireOp",EDGE,"E80"),sQuery(id+"F8.wireOp",EDGE,"E81"),sQuery(id+"F8.wireOp",EDGE,"E82"),sQuery(id+"F8.wireOp",EDGE,"E83"),sQuery(id+"F8.wireOp",EDGE,"E84"),sQuery(id+"F8.wireOp",EDGE,"E85")])],"isStart":true});
            var sketch = newSketch(context, id + "F14", { "sketchPlane" : qUnion([Q0])});
            skLineSegment(sketch, "E124", {"start": v(31.6, 177.8) * mm, "end": v(31.6, 182.88) * mm, "construction": true});
            skLineSegment(sketch, "E125", {"start": v(31.6, 182.88) * mm, "end": v(145.9, 182.88) * mm});
            skLineSegment(sketch, "E126", {"start": v(31.6, 182.88) * mm, "end": v(30.96, 182.88) * mm, "construction": true});
            skLineSegment(sketch, "E127", {"start": v(30.96, 182.88) * mm, "end": v(30.96, 177.8) * mm});
            skLineSegment(sketch, "E128", {"start": v(30.96, 177.8) * mm, "end": v(32.23, 177.8) * mm});
            skLineSegment(sketch, "E129", {"start": v(32.23, 177.8) * mm, "end": v(32.23, 181.61) * mm});
            skLineSegment(sketch, "E130", {"start": v(32.23, 181.61) * mm, "end": v(94.77, 181.61) * mm});
            skLineSegment(sketch, "E131", {"start": v(145.9, 181.61) * mm, "end": v(145.9, 182.88) * mm});
            skLineSegment(sketch, "E132", {"start": v(95.4, 177.8) * mm, "end": v(95.4, 181.61) * mm, "construction": true});
            skLineSegment(sketch, "E133", {"start": v(96.04, 181.61) * mm, "end": v(96.04, 177.8) * mm});
            skLineSegment(sketch, "E134", {"start": v(94.77, 177.8) * mm, "end": v(94.77, 181.61) * mm});
            skLineSegment(sketch, "E135.trimOffspring", {"start": v(95.4, 181.61) * mm, "end": v(145.9, 181.61) * mm});
            skLineSegment(sketch, "E136", {"start": v(94.77, 177.8) * mm, "end": v(96.04, 177.8) * mm});
            skLineSegment(sketch, "E137", {"start": v(32.23, 177.8) * mm, "end": v(30.96, 177.8) * mm});
            skLineSegment(sketch, "E138", {"start": v(31.6, 182.88) * mm, "end": v(30.96, 182.88) * mm});
            skSolve(sketch);
        }
        {
            var Q0;
            Q0 = qSketchRegion(id + "F14", true);
            extrude(context, id + "F15", {"entities" : qUnion([Q0]), "oppositeDirection" : true, "depth" : 109.22 * mm, "offsetDistance" : 25.4 * mm});
        }
        {
            var Q0;
            {var subQ0=sQuery(id+"F0.wireOp",EDGE,"E2");var subQ2=sQuery(id+"F0.wireOp",EDGE,"E6.0");var subQ4=sQuery(id+"F2.wireOp",EDGE,"E44.MirrorCS");var subQ5=sQuery(id+"F2.wireOp",EDGE,"E35.0");var subQ6=sQuery(id+"F2.wireOp",EDGE,"E22.0");var subQ7=sQuery(id+"F2.wireOp",EDGE,"E15.MirrorCS");var subQ8=sQuery(id+"F2.wireOp",EDGE,"E47");var subQ9=sQuery(id+"F2.wireOp",EDGE,"E37.0");var subQ10=sQuery(id+"F0.wireOp",EDGE,"E1");var subQ11=sQuery(id+"F2.wireOp",EDGE,"E45.MirrorCS");var subQ12=sQuery(id+"F2.wireOp",EDGE,"E39");var subQ13=sQuery(id+"F2.wireOp",EDGE,"E16.MirrorCS");var subQ14=sQuery(id+"F0.wireOp",EDGE,"E3");var subQ15=sQuery(id+"F0.wireOp",EDGE,"E0");var subQ16=sQuery(id+"F2.wireOp",EDGE,"E17");var subQ17=sQuery(id+"F0.wireOp",EDGE,"E4.0");var subQ18=sQuery(id+"F0.wireOp",EDGE,"E5.0");var subQ19=sQuery(id+"F2.wireOp",EDGE,"E43.MirrorCS");var subQ20=sQuery(id+"F2.wireOp",EDGE,"E18.MirrorCS");var subQ21=sQuery(id+"F0.wireOp",EDGE,"E7.0");var subQ22=sQuery(id+"F2.wireOp",EDGE,"E23.0");var subQ23=sQuery(id+"F2.wireOp",EDGE,"E11.0");var subQ24=sQuery(id+"F2.wireOp",EDGE,"E27");var subQ25=sQuery(id+"F2.wireOp",EDGE,"E12");Q0=makeQuery(id+"F13.boolean.opBoolean","SPLIT",FACE,{"disambiguationData":[TD([makeQuery(id+"F13.opExtrude","SWEPT_FACE",FACE,{"disambiguationData":[OSD([sQuery(id+"F12.wireOp",EDGE,"E119")])]})])],"derivedFrom":makeQuery(id+"F11.boolean.opBoolean","MERGE",FACE,{"derivedFrom":[makeQuery(id+"F7.boolean.opBoolean","SPLIT",FACE,{"disambiguationData":[TD([makeQuery(id+"F1.opExtrude","SWEPT_FACE",FACE,{"disambiguationData":[OSD([subQ15])]})])],"derivedFrom":makeQuery(id+"F3.boolean.opBoolean","MERGE",FACE,{"derivedFrom":[makeQuery(id+"F1.opExtrude","CAP_FACE",FACE,{"disambiguationData":[OSD([subQ15,subQ10,subQ0,subQ14,subQ17,subQ18,subQ2,subQ21])],"isStart":false}),makeQuery(id+"F3.opExtrude","CAP_FACE",FACE,{"disambiguationData":[OSD([sQuery(id+"F2.wireOp",EDGE,"E9"),sQuery(id+"F2.wireOp",EDGE,"E10"),sQuery(id+"F2.wireOp",EDGE,"E40.MirrorCS"),sQuery(id+"F2.wireOp",EDGE,"E41.MirrorCS"),sQuery(id+"F2.wireOp",EDGE,"E42.MirrorCS"),sQuery(id+"F2.wireOp",EDGE,"E53")])],"isStart":false}),makeQuery(id+"F3.opExtrude","CAP_FACE",FACE,{"disambiguationData":[OSD([subQ23,subQ25,subQ19,subQ4,subQ11,sQuery(id+"F2.wireOp",EDGE,"E52")])],"isStart":false}),makeQuery(id+"F3.opExtrude","CAP_FACE",FACE,{"disambiguationData":[OSD([sQuery(id+"F2.wireOp",EDGE,"E13.MirrorCS"),sQuery(id+"F2.wireOp",EDGE,"E14.MirrorCS"),sQuery(id+"F2.wireOp",EDGE,"E31.0"),sQuery(id+"F2.wireOp",EDGE,"E36.0"),sQuery(id+"F2.wireOp",EDGE,"E38"),sQuery(id+"F2.wireOp",EDGE,"E50")])],"isStart":false}),makeQuery(id+"F3.opExtrude","CAP_FACE",FACE,{"disambiguationData":[OSD([subQ7,subQ13,subQ5,subQ9,subQ12,sQuery(id+"F2.wireOp",EDGE,"E51")])],"isStart":false}),makeQuery(id+"F3.opExtrude","CAP_FACE",FACE,{"disambiguationData":[OSD([subQ16,subQ6,subQ8,sQuery(id+"F2.wireOp",EDGE,"E49")])],"isStart":false}),makeQuery(id+"F3.opExtrude","CAP_FACE",FACE,{"disambiguationData":[OSD([subQ20,subQ22,subQ24,sQuery(id+"F2.wireOp",EDGE,"E48")])],"isStart":false})]})}),makeQuery(id+"F11.opExtrude","CAP_FACE",FACE,{"disambiguationData":[OSD([sQuery(id+"F10.wireOp",EDGE,"E97.top"),sQuery(id+"F10.wireOp",EDGE,"E98.top"),sQuery(id+"F10.wireOp",EDGE,"E98.left"),sQuery(id+"F10.wireOp",EDGE,"E98.right"),sQuery(id+"F10.wireOp",EDGE,"E99"),sQuery(id+"F10.wireOp",EDGE,"E100"),sQuery(id+"F10.wireOp",EDGE,"E101"),sQuery(id+"F10.wireOp",EDGE,"E102"),sQuery(id+"F10.wireOp",EDGE,"E104"),sQuery(id+"F10.wireOp",EDGE,"E105"),sQuery(id+"F10.wireOp",EDGE,"E106"),sQuery(id+"F10.wireOp",EDGE,"E107.1.0.0"),sQuery(id+"F10.wireOp",EDGE,"E107.1.0.1"),sQuery(id+"F10.wireOp",EDGE,"E107.1.0.2"),sQuery(id+"F10.wireOp",EDGE,"E107.2.0.0"),sQuery(id+"F10.wireOp",EDGE,"E107.2.0.1"),sQuery(id+"F10.wireOp",EDGE,"E107.2.0.2"),sQuery(id+"F10.wireOp",EDGE,"E107.3.0.0"),sQuery(id+"F10.wireOp",EDGE,"E107.3.0.1"),sQuery(id+"F10.wireOp",EDGE,"E107.3.0.2")])],"isStart":true})]})});}
            var sketch = newSketch(context, id + "F16", { "sketchPlane" : qUnion([Q0])});
            skLineSegment(sketch, "E139", {"start": v(134.62, 12.7) * mm, "end": v(134.62, 10.16) * mm});
            skLineSegment(sketch, "E140", {"start": v(134.62, 10.16) * mm, "end": v(144.78, 10.16) * mm});
            skLineSegment(sketch, "E141", {"start": v(144.78, 12.7) * mm, "end": v(144.78, 101.6) * mm});
            skLineSegment(sketch, "E142", {"start": v(144.78, 101.6) * mm, "end": v(134.62, 101.6) * mm});
            skLineSegment(sketch, "E143", {"start": v(134.62, 101.6) * mm, "end": v(134.62, 99.06) * mm});
            skLineSegment(sketch, "E144", {"start": v(134.62, 99.06) * mm, "end": v(142.24, 99.06) * mm});
            skLineSegment(sketch, "E145", {"start": v(142.24, 99.06) * mm, "end": v(142.24, 63.5) * mm});
            skLineSegment(sketch, "E146", {"start": v(142.24, 63.5) * mm, "end": v(134.62, 63.5) * mm});
            skLineSegment(sketch, "E147", {"start": v(134.62, 63.5) * mm, "end": v(134.62, 60.96) * mm});
            skLineSegment(sketch, "E148", {"start": v(134.62, 60.96) * mm, "end": v(142.24, 60.96) * mm});
            skLineSegment(sketch, "E149", {"start": v(142.24, 60.96) * mm, "end": v(142.24, 12.7) * mm});
            skLineSegment(sketch, "E150", {"start": v(142.24, 12.7) * mm, "end": v(134.62, 12.7) * mm});
            skLineSegment(sketch, "E151", {"start": v(144.78, 10.16) * mm, "end": v(152.4, 10.16) * mm});
            skLineSegment(sketch, "E152", {"start": v(152.4, 10.16) * mm, "end": v(152.4, 12.7) * mm});
            skLineSegment(sketch, "E153", {"start": v(152.4, 12.7) * mm, "end": v(144.78, 12.7) * mm});
            skSolve(sketch);
        }
        {
            var Q0;
            Q0=makeQuery(id+"F16.imprint","IMPRINT",FACE,{"disambiguationData":[TD([[makeQuery(id+"F16.imprint","IMPRINT",EDGE,{"derivedFrom":sQuery(id+"F16.wireOp",EDGE,"E139")}),1.0]])]});
            extrude(context, id + "F17", {"entities" : qUnion([Q0]), "oppositeDirection" : true, "depth" : 109.22 * mm, "offsetDistance" : 25.4 * mm});
        }
        {
            var Q0;
            {var subQ0=sQuery(id+"F2.wireOp",EDGE,"E23.0");var subQ2=sQuery(id+"F2.wireOp",EDGE,"E27");var subQ4=sQuery(id+"F2.wireOp",EDGE,"E18.MirrorCS");var subQ6=sQuery(id+"F0.wireOp",EDGE,"E7.0");var subQ8=sQuery(id+"F2.wireOp",EDGE,"E35.0");var subQ10=sQuery(id+"F2.wireOp",EDGE,"E15.MirrorCS");var subQ11=makeQuery(id+"F3.opExtrude","SWEPT_FACE",FACE,{"disambiguationData":[OSD([subQ10])]});var subQ12=sQuery(id+"F0.wireOp",EDGE,"E1");var subQ14=sQuery(id+"F2.wireOp",EDGE,"E37.0");var subQ16=sQuery(id+"F0.wireOp",EDGE,"E6.0");var subQ18=sQuery(id+"F0.wireOp",EDGE,"E2");var subQ20=sQuery(id+"F2.wireOp",EDGE,"E16.MirrorCS");var subQ22=sQuery(id+"F2.wireOp",EDGE,"E39");var subQ25=sQuery(id+"F2.wireOp",EDGE,"E44.MirrorCS");var subQ26=sQuery(id+"F2.wireOp",EDGE,"E22.0");var subQ27=sQuery(id+"F2.wireOp",EDGE,"E47");var subQ28=sQuery(id+"F2.wireOp",EDGE,"E45.MirrorCS");var subQ29=sQuery(id+"F0.wireOp",EDGE,"E3");var subQ30=sQuery(id+"F0.wireOp",EDGE,"E0");var subQ31=sQuery(id+"F2.wireOp",EDGE,"E17");var subQ32=sQuery(id+"F0.wireOp",EDGE,"E4.0");var subQ33=sQuery(id+"F0.wireOp",EDGE,"E5.0");var subQ34=sQuery(id+"F2.wireOp",EDGE,"E43.MirrorCS");var subQ35=sQuery(id+"F2.wireOp",EDGE,"E11.0");var subQ36=sQuery(id+"F2.wireOp",EDGE,"E12");Q0=makeQuery(id+"F13.boolean.opBoolean","SPLIT",FACE,{"disambiguationData":[TD([subQ11])],"derivedFrom":makeQuery(id+"F11.boolean.opBoolean","MERGE",FACE,{"derivedFrom":[makeQuery(id+"F7.boolean.opBoolean","SPLIT",FACE,{"disambiguationData":[TD([makeQuery(id+"F1.opExtrude","SWEPT_FACE",FACE,{"disambiguationData":[OSD([subQ30])]})])],"derivedFrom":makeQuery(id+"F3.boolean.opBoolean","MERGE",FACE,{"derivedFrom":[makeQuery(id+"F1.opExtrude","CAP_FACE",FACE,{"disambiguationData":[OSD([subQ30,subQ12,subQ18,subQ29,subQ32,subQ33,subQ16,subQ6])],"isStart":false}),makeQuery(id+"F3.opExtrude","CAP_FACE",FACE,{"disambiguationData":[OSD([sQuery(id+"F2.wireOp",EDGE,"E9"),sQuery(id+"F2.wireOp",EDGE,"E10"),sQuery(id+"F2.wireOp",EDGE,"E40.MirrorCS"),sQuery(id+"F2.wireOp",EDGE,"E41.MirrorCS"),sQuery(id+"F2.wireOp",EDGE,"E42.MirrorCS"),sQuery(id+"F2.wireOp",EDGE,"E53")])],"isStart":false}),makeQuery(id+"F3.opExtrude","CAP_FACE",FACE,{"disambiguationData":[OSD([subQ35,subQ36,subQ34,subQ25,subQ28,sQuery(id+"F2.wireOp",EDGE,"E52")])],"isStart":false}),makeQuery(id+"F3.opExtrude","CAP_FACE",FACE,{"disambiguationData":[OSD([sQuery(id+"F2.wireOp",EDGE,"E13.MirrorCS"),sQuery(id+"F2.wireOp",EDGE,"E14.MirrorCS"),sQuery(id+"F2.wireOp",EDGE,"E31.0"),sQuery(id+"F2.wireOp",EDGE,"E36.0"),sQuery(id+"F2.wireOp",EDGE,"E38"),sQuery(id+"F2.wireOp",EDGE,"E50")])],"isStart":false}),makeQuery(id+"F3.opExtrude","CAP_FACE",FACE,{"disambiguationData":[OSD([subQ10,subQ20,subQ8,subQ14,subQ22,sQuery(id+"F2.wireOp",EDGE,"E51")])],"isStart":false}),makeQuery(id+"F3.opExtrude","CAP_FACE",FACE,{"disambiguationData":[OSD([subQ31,subQ26,subQ27,sQuery(id+"F2.wireOp",EDGE,"E49")])],"isStart":false}),makeQuery(id+"F3.opExtrude","CAP_FACE",FACE,{"disambiguationData":[OSD([subQ4,subQ0,subQ2,sQuery(id+"F2.wireOp",EDGE,"E48")])],"isStart":false})]})}),makeQuery(id+"F11.opExtrude","CAP_FACE",FACE,{"disambiguationData":[OSD([sQuery(id+"F10.wireOp",EDGE,"E97.top"),sQuery(id+"F10.wireOp",EDGE,"E99"),sQuery(id+"F10.wireOp",EDGE,"E100"),sQuery(id+"F10.wireOp",EDGE,"E101"),sQuery(id+"F10.wireOp",EDGE,"E102"),sQuery(id+"F10.wireOp",EDGE,"E104"),sQuery(id+"F10.wireOp",EDGE,"E105"),sQuery(id+"F10.wireOp",EDGE,"E106"),sQuery(id+"F10.wireOp",EDGE,"E107.1.0.0"),sQuery(id+"F10.wireOp",EDGE,"E107.1.0.1"),sQuery(id+"F10.wireOp",EDGE,"E107.1.0.2"),sQuery(id+"F10.wireOp",EDGE,"E107.2.0.0"),sQuery(id+"F10.wireOp",EDGE,"E107.2.0.1"),sQuery(id+"F10.wireOp",EDGE,"E107.2.0.2"),sQuery(id+"F10.wireOp",EDGE,"E107.3.0.0"),sQuery(id+"F10.wireOp",EDGE,"E107.3.0.1"),sQuery(id+"F10.wireOp",EDGE,"E107.3.0.2"),sQuery(id+"F10.wireOp",EDGE,"E108"),sQuery(id+"F10.wireOp",EDGE,"E109"),sQuery(id+"F10.wireOp",EDGE,"E110"),sQuery(id+"F10.wireOp",EDGE,"E111")])],"isStart":true}),makeQuery(id+"F11.opExtrude","CAP_FACE",FACE,{"disambiguationData":[OSD([sQuery(id+"F10.wireOp",EDGE,"E112"),sQuery(id+"F10.wireOp",EDGE,"E113"),sQuery(id+"F10.wireOp",EDGE,"E114"),sQuery(id+"F10.wireOp",EDGE,"E115")])],"isStart":true})]})});}
            var sketch = newSketch(context, id + "F18", { "sketchPlane" : qUnion([Q0])});
            skLineSegment(sketch, "E154", {"start": v(134.62, 164.61) * mm, "end": v(147.32, 164.61) * mm});
            skLineSegment(sketch, "E155", {"start": v(147.32, 164.61) * mm, "end": v(147.32, 162.07) * mm});
            skLineSegment(sketch, "E156", {"start": v(147.32, 162.07) * mm, "end": v(134.62, 162.07) * mm});
            skLineSegment(sketch, "E157", {"start": v(134.62, 162.07) * mm, "end": v(134.62, 164.61) * mm});
            skSolve(sketch);
        }
        {
            var Q0;
            Q0 = qSketchRegion(id + "F18", true);
            extrude(context, id + "F19", {"entities" : qUnion([Q0]), "oppositeDirection" : true, "depth" : 109.22 * mm, "offsetDistance" : 25.4 * mm});
        }
    });
